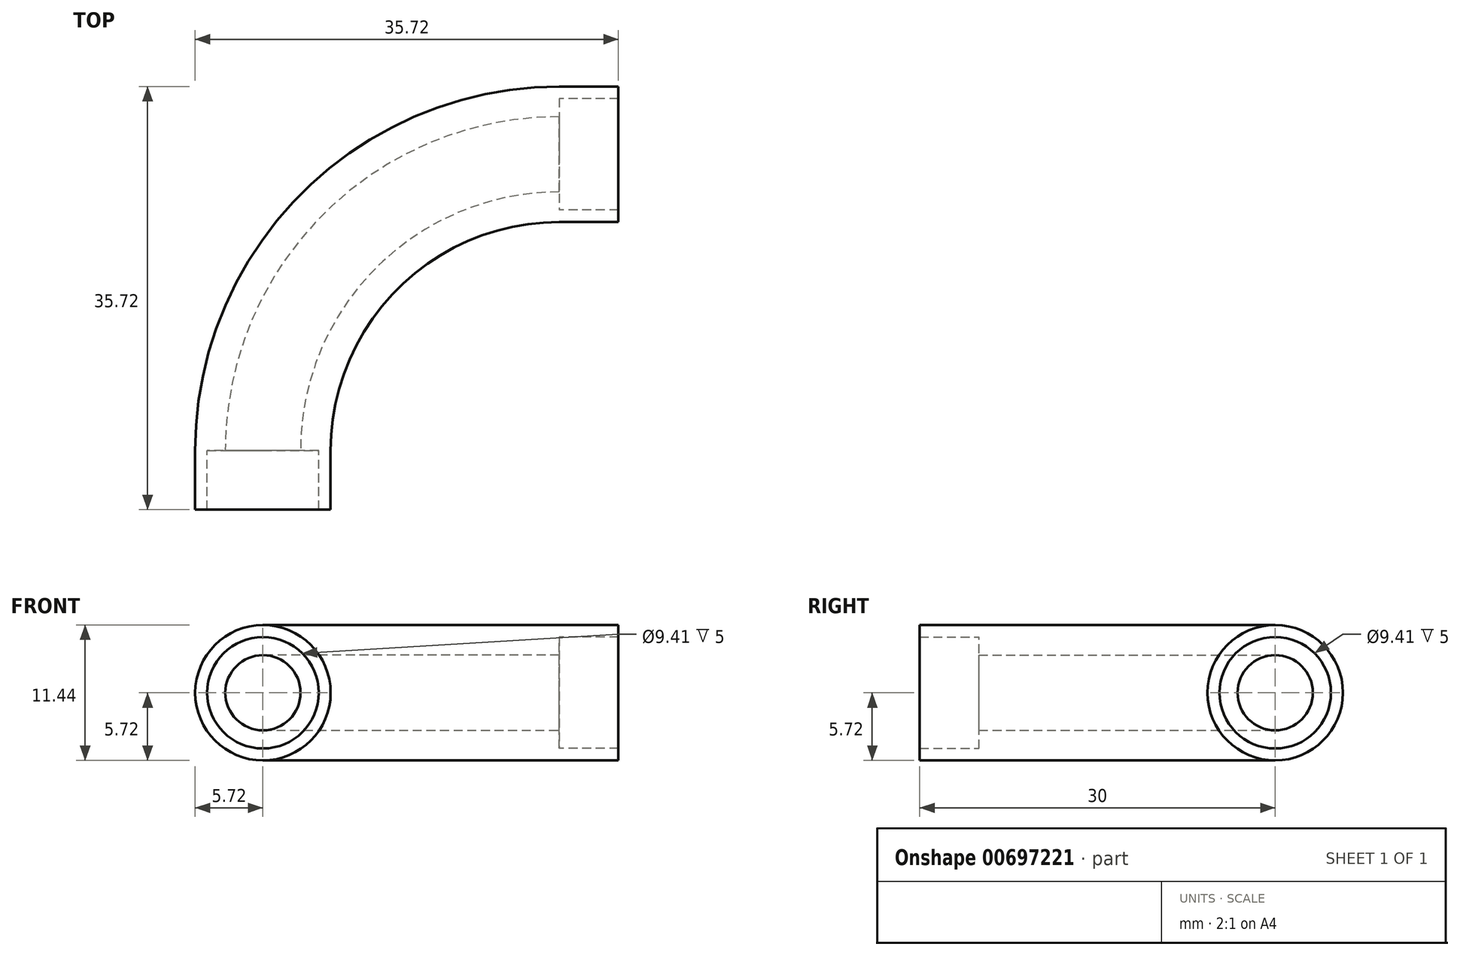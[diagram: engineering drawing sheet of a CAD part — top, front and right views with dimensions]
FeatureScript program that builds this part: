
annotation { "Feature Type Name" : "Feature", "Feature Type Description" : "" }
export const myFeature = defineFeature(function(context is Context, id is Id, definition is map)
    precondition{}
    {
        {
            var Q0;
            Q0=qCreatedBy(makeId("Top.planeOp"),FACE);
            var sketch = newSketch(context, id + "F0", { "sketchPlane" : qUnion([Q0])});
            skArc(sketch, "E0", {"start": v(-25, 0) * mm, "mid": v(-17.68, 17.68) * mm, "end": v(0, 25) * mm});
            skSolve(sketch);
        }
        {
            var Q0;
            Q0=qCreatedBy(makeId("Front.planeOp"),FACE);
            var sketch = newSketch(context, id + "F1", { "sketchPlane" : qUnion([Q0])});
            skCircle(sketch, "E1", {"center": v(-25, 0) * mm, "radius": 3.17 * mm});
            skCircle(sketch, "E2", {"center": v(-25, 0) * mm, "radius": 5.71 * mm});
            skSolve(sketch);
        }
        {
            var Q0;
            Q0=makeQuery(id+"F1.imprint","IMPRINT",FACE,{"disambiguationData":[TD([[makeQuery(id+"F1.imprint","IMPRINT",EDGE,{"derivedFrom":sQuery(id+"F1.wireOp",EDGE,"E1")}),-1.0]])]});
            var Q1;
            Q1=sQuery(id+"F0.wireOp",EDGE,"E0");
            sweep(context, id + "F2", {"profiles" : qUnion([Q0]), "path" : qUnion([Q1])});
        }
        {
            var Q0;
            Q0=makeQuery(id+"F2.opSweep","CAP_FACE",FACE,{"disambiguationData":[OSD([sQuery(id+"F0.wireOp",VERTEX,"E0.start"),sQuery(id+"F1.wireOp",EDGE,"E1"),sQuery(id+"F1.wireOp",EDGE,"E2")])],"isStart":true});
            var sketch = newSketch(context, id + "F3", { "sketchPlane" : qUnion([Q0])});
            skCircle(sketch, "E3", {"center": v(-25, 0) * mm, "radius": 4.7 * mm});
            skCircle(sketch, "E4", {"center": v(-25, 0) * mm, "radius": 5.71 * mm});
            skSolve(sketch);
        }
        {
            var Q0;
            Q0 = qSketchRegion(id + "F3", true);
            extrude(context, id + "F4", {"entities" : qUnion([Q0]), "operationType" : NewBodyOperationType.ADD, "depth" : 5 * mm, "offsetDistance" : 25 * mm});
        }
        {
            var Q0;
            Q0=makeQuery(id+"F2.opSweep","CAP_FACE",FACE,{"disambiguationData":[OSD([sQuery(id+"F0.wireOp",VERTEX,"E0.end"),sQuery(id+"F1.wireOp",EDGE,"E1"),sQuery(id+"F1.wireOp",EDGE,"E2")])],"isStart":false});
            var sketch = newSketch(context, id + "F5", { "sketchPlane" : qUnion([Q0])});
            skCircle(sketch, "E5", {"center": v(25, 0) * mm, "radius": 5.71 * mm});
            skCircle(sketch, "E6", {"center": v(25, 0) * mm, "radius": 4.7 * mm});
            skSolve(sketch);
        }
        {
            var Q0;
            Q0=makeQuery(id+"F5.imprint","IMPRINT",FACE,{"disambiguationData":[TD([[makeQuery(id+"F5.imprint","IMPRINT",EDGE,{"derivedFrom":sQuery(id+"F5.wireOp",EDGE,"E5")}),1.0]])]});
            extrude(context, id + "F6", {"entities" : qUnion([Q0]), "operationType" : NewBodyOperationType.ADD, "depth" : 5 * mm, "offsetDistance" : 25 * mm});
        }
    });
